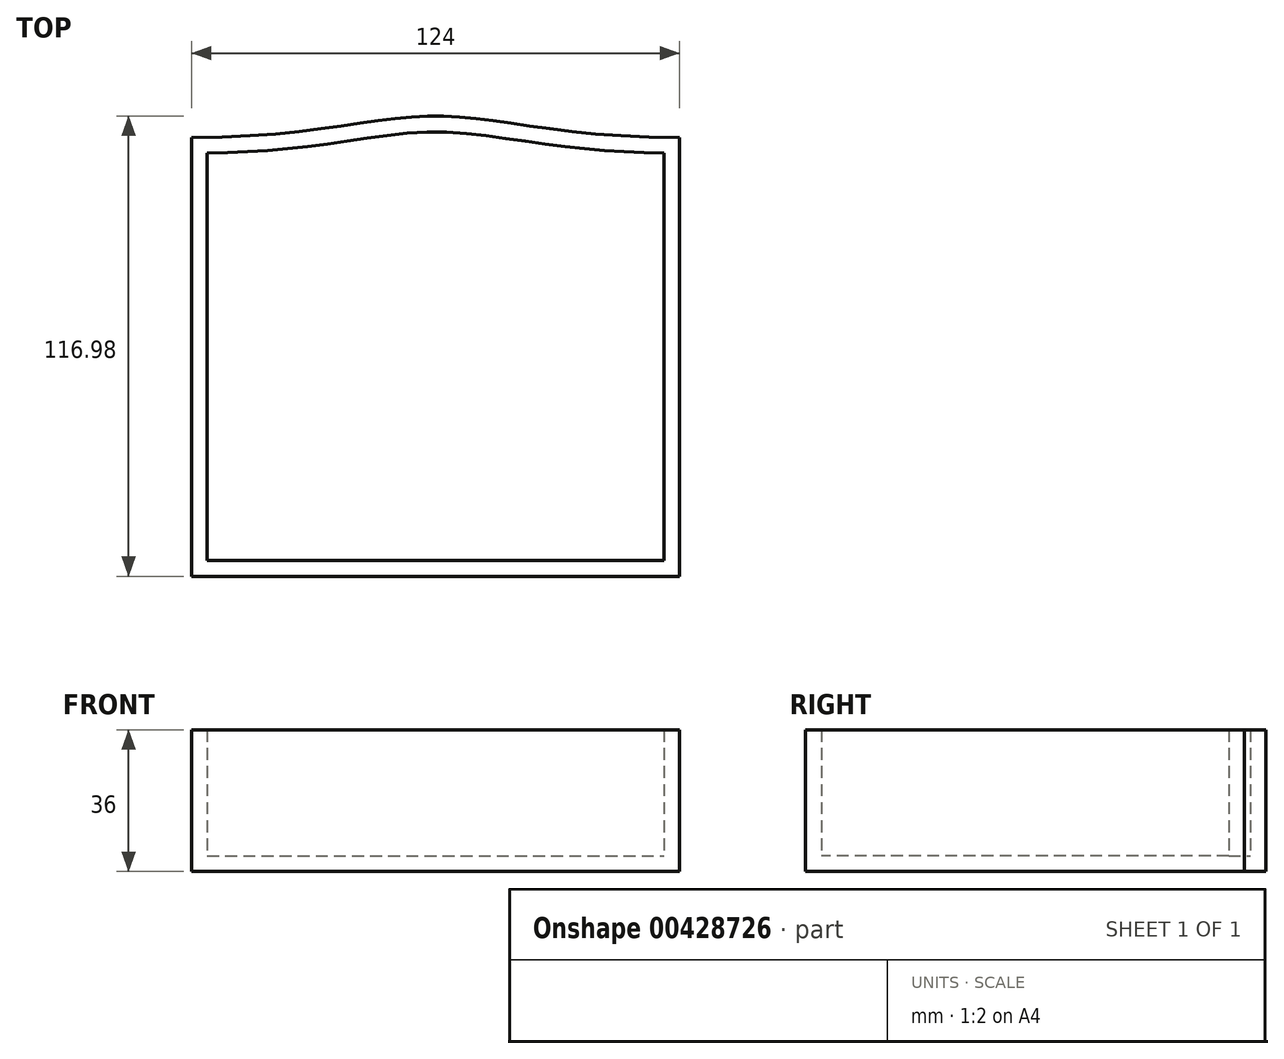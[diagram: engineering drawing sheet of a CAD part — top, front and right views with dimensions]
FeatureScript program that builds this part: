
annotation { "Feature Type Name" : "Feature", "Feature Type Description" : "" }
export const myFeature = defineFeature(function(context is Context, id is Id, definition is map)
    precondition{}
    {
        {
            assignVariable(context, id + "F0", {"name" : "Height", "anyValue" : 40});
        }
        {
            assignVariable(context, id + "F1", {"name" : "WallThickness", "anyValue" : 4});
        }
        {
            var Q0;
            Q0=qCreatedBy(makeId("Top.planeOp"),FACE);
            var sketch = newSketch(context, id + "F2", { "sketchPlane" : qUnion([Q0])});
            skLineSegment(sketch, "E0", {"start": v(0, 111.5) * mm, "end": v(0, 0) * mm});
            skLineSegment(sketch, "E1", {"start": v(0, 0) * mm, "end": v(124, 0) * mm});
            skLineSegment(sketch, "E2", {"start": v(124, 0) * mm, "end": v(124, 111.5) * mm});
            skFitSpline(sketch, "E3", {"points": [v(0, 111.5) * mm, v(62, 116.98) * mm, v(124, 111.5) * mm], "startDerivative": vector(186, 0) * mm, "endDerivative": vector(186, 0) * mm});
            skLineSegment(sketch, "E4", {"start": v(124, 111.5) * mm, "end": v(93, 111.5) * mm, "construction": true});
            skLineSegment(sketch, "E5", {"start": v(31, 111.5) * mm, "end": v(0, 111.5) * mm, "construction": true});
            skLineSegment(sketch, "E6", {"start": v(93, 111.5) * mm, "end": v(62, 111.5) * mm, "construction": true});
            skLineSegment(sketch, "E7", {"start": v(62, 111.5) * mm, "end": v(31, 111.5) * mm, "construction": true});
            skSolve(sketch);
        }
        {
            var Q0;
            Q0=makeQuery(id+"F2.imprint","IMPRINT",FACE,{"disambiguationData":[TD([[makeQuery(id+"F2.imprint","IMPRINT",EDGE,{"derivedFrom":sQuery(id+"F2.wireOp",EDGE,"E0")}),1.0]])]});
            extrude(context, id + "F3", {"entities" : qUnion([Q0]), "depth" : (getVariable(context, 'Height') - getVariable(context, 'WallThickness')) * mm});
        }
        {
            var Q0;
            Q0=makeQuery(id+"F3.opExtrude","CAP_FACE",FACE,{"disambiguationData":[OSD([sQuery(id+"F2.wireOp",EDGE,"E0"),sQuery(id+"F2.wireOp",EDGE,"E1"),sQuery(id+"F2.wireOp",EDGE,"E2"),sQuery(id+"F2.wireOp",EDGE,"E3")])],"isStart":false});
            shell(context, id + "F4", {"entities" : qUnion([Q0]), "thickness" : (getVariable(context, 'WallThickness')) * mm});
        }
    });
